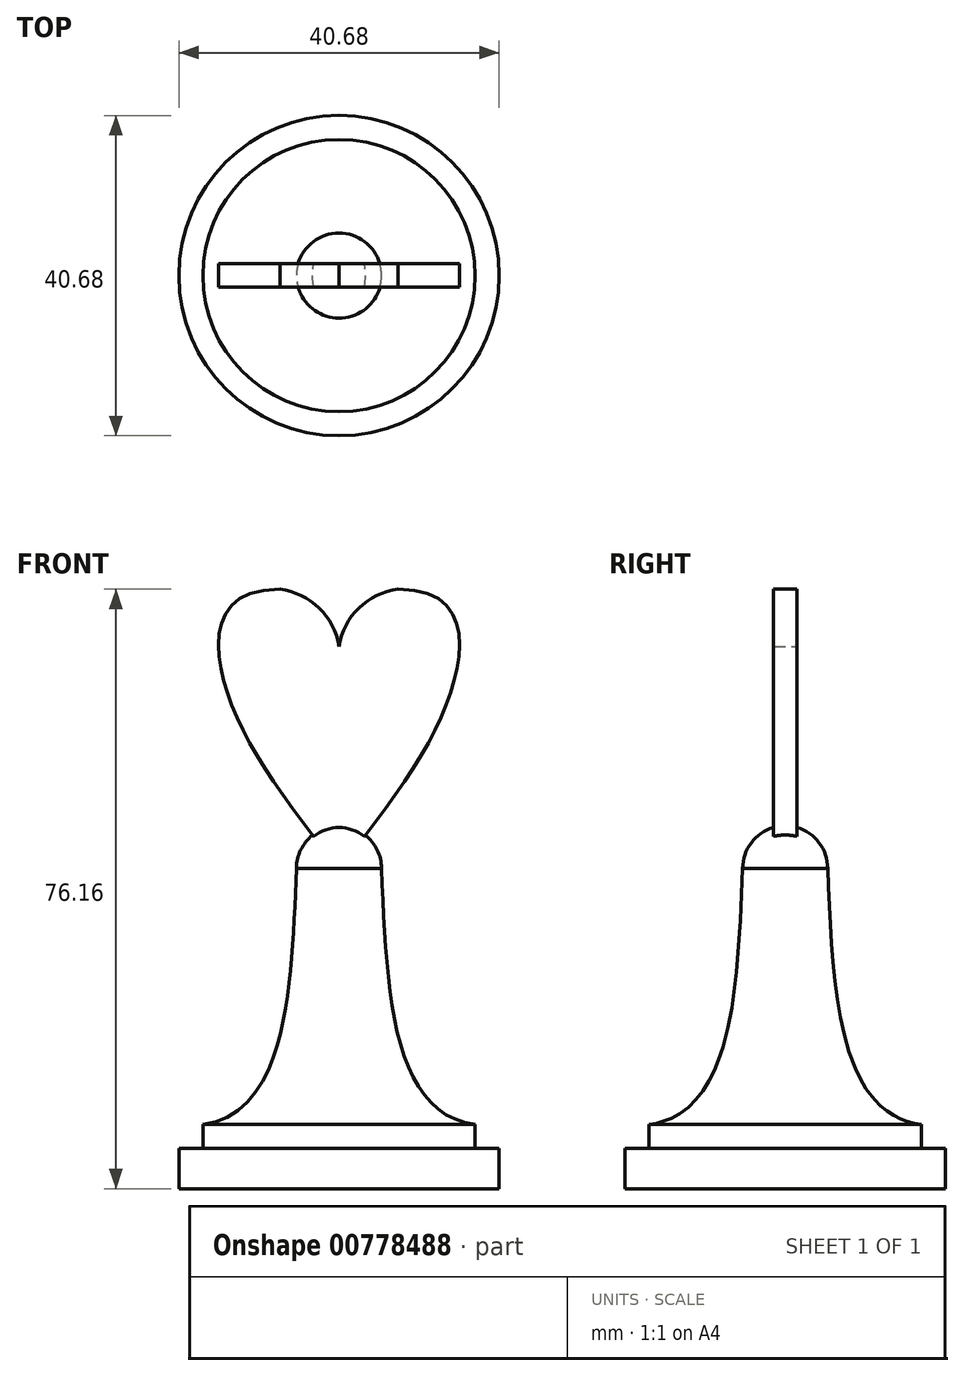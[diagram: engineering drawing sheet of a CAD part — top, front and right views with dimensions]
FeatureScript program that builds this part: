
annotation { "Feature Type Name" : "Feature", "Feature Type Description" : "" }
export const myFeature = defineFeature(function(context is Context, id is Id, definition is map)
    precondition{}
    {
        {
            var Q0;
            Q0=qCreatedBy(makeId("Front.planeOp"),FACE);
            var sketch = newSketch(context, id + "F0", { "sketchPlane" : qUnion([Q0])});
            skLineSegment(sketch, "E0", {"start": v(-20.34, -40.69) * mm, "end": v(0, -40.69) * mm});
            skLineSegment(sketch, "E1", {"start": v(-20.34, -40.69) * mm, "end": v(-20.34, -35.6) * mm});
            skLineSegment(sketch, "E2", {"start": v(-17.3, -32.55) * mm, "end": v(-17.3, -35.6) * mm});
            skLineSegment(sketch, "E3", {"start": v(-20.34, -35.6) * mm, "end": v(-17.3, -35.6) * mm});
            skArc(sketch, "E4", {"start": v(0, 5.4) * mm, "mid": v(-3.82, 3.82) * mm, "end": v(-5.4, 0) * mm});
            skFitSpline(sketch, "E5", {"points": [v(-5.4, 0) * mm, v(-17.3, -32.55) * mm, v(-46.59, -25.78) * mm, v(-42.81, -32.55) * mm, v(-43.07, -32.55) * mm], "startDerivative": vector(-4.71, -116.07) * mm, "endDerivative": vector(-11.27, 4.12) * mm});
            skLineSegment(sketch, "E6", {"start": v(0, 5.4) * mm, "end": v(0, -40.69) * mm});
            skLineSegment(sketch, "E7", {"start": v(0, 27.07) * mm, "end": v(0, -57.22) * mm});
            skSolve(sketch);
        }
        {
            var Q0;
            {var subQ0=sQuery(id+"F0.wireOp",EDGE,"E0");Q0=makeQuery(id+"F0.imprint","IMPRINT",FACE,{"disambiguationData":[TD([[makeQuery(id+"F0.imprint","IMPRINT",EDGE,{"derivedFrom":subQ0}),1.0]])]});}
            var Q1;
            Q1 = qSketchRegion(id + "F0", true);
            var Q2;
            Q2=sQuery(id+"F0.wireOp",EDGE,"E7");
            revolve(context, id + "F1", {"surfaceOperationType" : NewSurfaceOperationType.NEW, "entities" : qUnion([Q0, Q1]), "axis" : qUnion([Q2]), "revolveType" : RevolveType.FULL});
        }
        {
            var Q0;
            Q0=qCreatedBy(makeId("Front.planeOp"),FACE);
            var sketch = newSketch(context, id + "F2", { "sketchPlane" : qUnion([Q0])});
            skLineSegment(sketch, "E8", {"start": v(0, 0) * mm, "end": v(0, 35.47) * mm});
            skArc(sketch, "E9", {"start": v(0, 25.47) * mm, "mid": v(-1.64, 32.05) * mm, "end": v(-7.5, 35.47) * mm});
            skFitSpline(sketch, "E10", {"points": [v(-7.5, 35.47) * mm, v(-15, 25.47) * mm, v(0, 0) * mm], "startDerivative": vector(-57.1, 0) * mm, "endDerivative": vector(38.02, -47.08) * mm});
            skSolve(sketch);
        }
        {
            var Q0;
            {var subQ0=sQuery(id+"F2.wireOp",EDGE,"E10");Q0=makeQuery(id+"F2.imprint","IMPRINT",FACE,{"disambiguationData":[TD([[makeQuery(id+"F2.imprint","IMPRINT",EDGE,{"derivedFrom":subQ0}),1.0]])]});}
            extrude(context, id + "F3", {"entities" : qUnion([Q0]), "operationType" : NewBodyOperationType.ADD, "endBound" : BoundingType.SYMMETRIC, "depth" : 3 * mm, "offsetDistance" : 25 * mm});
        }
        {
            var Q0;
            Q0=makeQuery(id+"F1.opRevolve","SWEPT_BODY",BODY,{"disambiguationData":[OSD([sQuery(id+"F0.wireOp",EDGE,"E0"),sQuery(id+"F0.wireOp",EDGE,"E1"),sQuery(id+"F0.wireOp",EDGE,"E2"),sQuery(id+"F0.wireOp",EDGE,"E3"),sQuery(id+"F0.wireOp",EDGE,"E4"),sQuery(id+"F0.wireOp",EDGE,"E5"),sQuery(id+"F0.wireOp",EDGE,"E7")])]});
            var Q1;
            Q1=qCreatedBy(makeId("Right.planeOp"),FACE);
            mirror(context, id + "F4", {"operationType" : NewBodyOperationType.ADD, "entities" : qUnion([Q0]), "mirrorPlane" : qUnion([Q1])});
        }
    });
